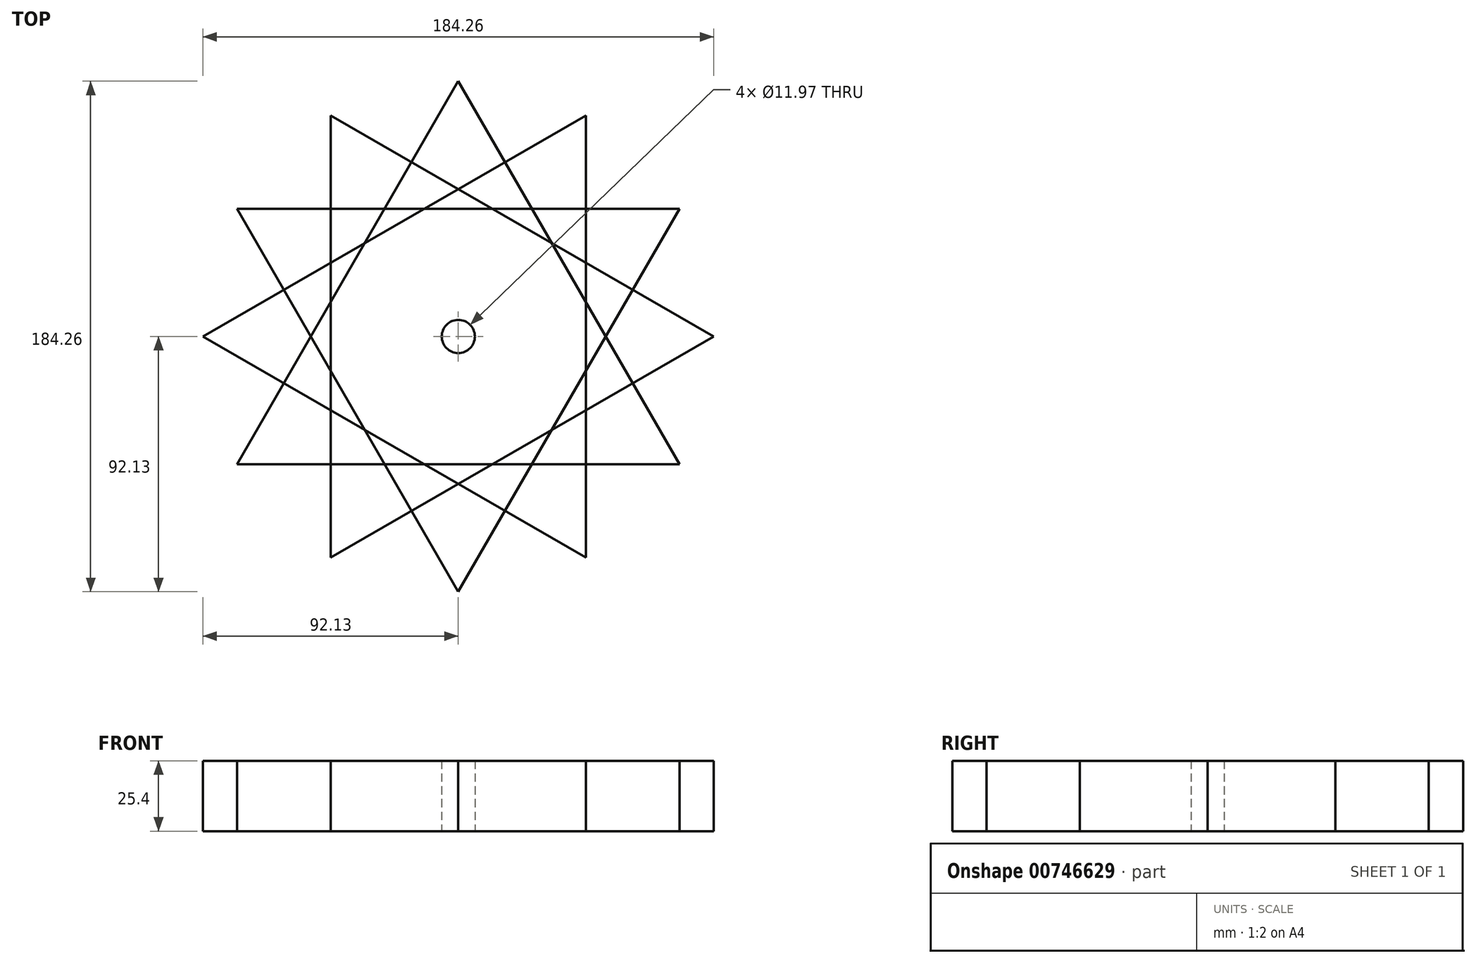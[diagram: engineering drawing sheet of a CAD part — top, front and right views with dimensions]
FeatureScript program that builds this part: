
annotation { "Feature Type Name" : "Feature", "Feature Type Description" : "" }
export const myFeature = defineFeature(function(context is Context, id is Id, definition is map)
    precondition{}
    {
        {
            var Q0;
            Q0=qCreatedBy(makeId("Top.planeOp"),FACE);
            var sketch = newSketch(context, id + "F0", { "sketchPlane" : qUnion([Q0])});
            skCircle(sketch, "E0", {"center": v(0, 0) * mm, "radius": 5.98 * mm});
            skCircle(sketch, "E1.cCircle", {"center": v(0, 0) * mm, "radius": 46.06 * mm, "construction": true});
            skLineSegment(sketch, "E1.0", {"start": v(-79.79, 46.06) * mm, "end": v(79.79, 46.06) * mm});
            skLineSegment(sketch, "E1.1", {"start": v(79.79, 46.06) * mm, "end": v(0, -92.13) * mm});
            skLineSegment(sketch, "E1.2", {"start": v(0, -92.13) * mm, "end": v(-79.79, 46.06) * mm});
            skPoint(sketch, "E1.0.midPoint", {"position": v(0, 46.06) * mm});
            skSolve(sketch);
        }
        {
            var Q0;
            Q0=makeQuery(id+"F0.imprint","IMPRINT",FACE,{"disambiguationData":[TD([[makeQuery(id+"F0.imprint","IMPRINT",EDGE,{"derivedFrom":sQuery(id+"F0.wireOp",EDGE,"E0")}),-1.0]])]});
            extrude(context, id + "F1", {"entities" : qUnion([Q0]), "depth" : 25.4 * mm, "offsetDistance" : 25.4 * mm});
        }
        {
            var Q0;
            Q0=makeQuery(id+"F1.opExtrude","SWEPT_BODY",BODY,{"disambiguationData":[OSD([sQuery(id+"F0.wireOp",EDGE,"E0"),sQuery(id+"F0.wireOp",EDGE,"E1.0"),sQuery(id+"F0.wireOp",EDGE,"E1.1"),sQuery(id+"F0.wireOp",EDGE,"E1.2")])]});
            var Q1;
            Q1=makeQuery(id+"F1.opExtrude","CAP_EDGE",EDGE,{"disambiguationData":[OSD([sQuery(id+"F0.wireOp",EDGE,"E0")])],"isStart":false});
            circularPattern(context, id + "F2", {"entities" : qUnion([Q0]), "axis" : qUnion([Q1]), "angle" : 360 * degree, "instanceCount" : 4, "equalSpace" : true});
        }
    });
